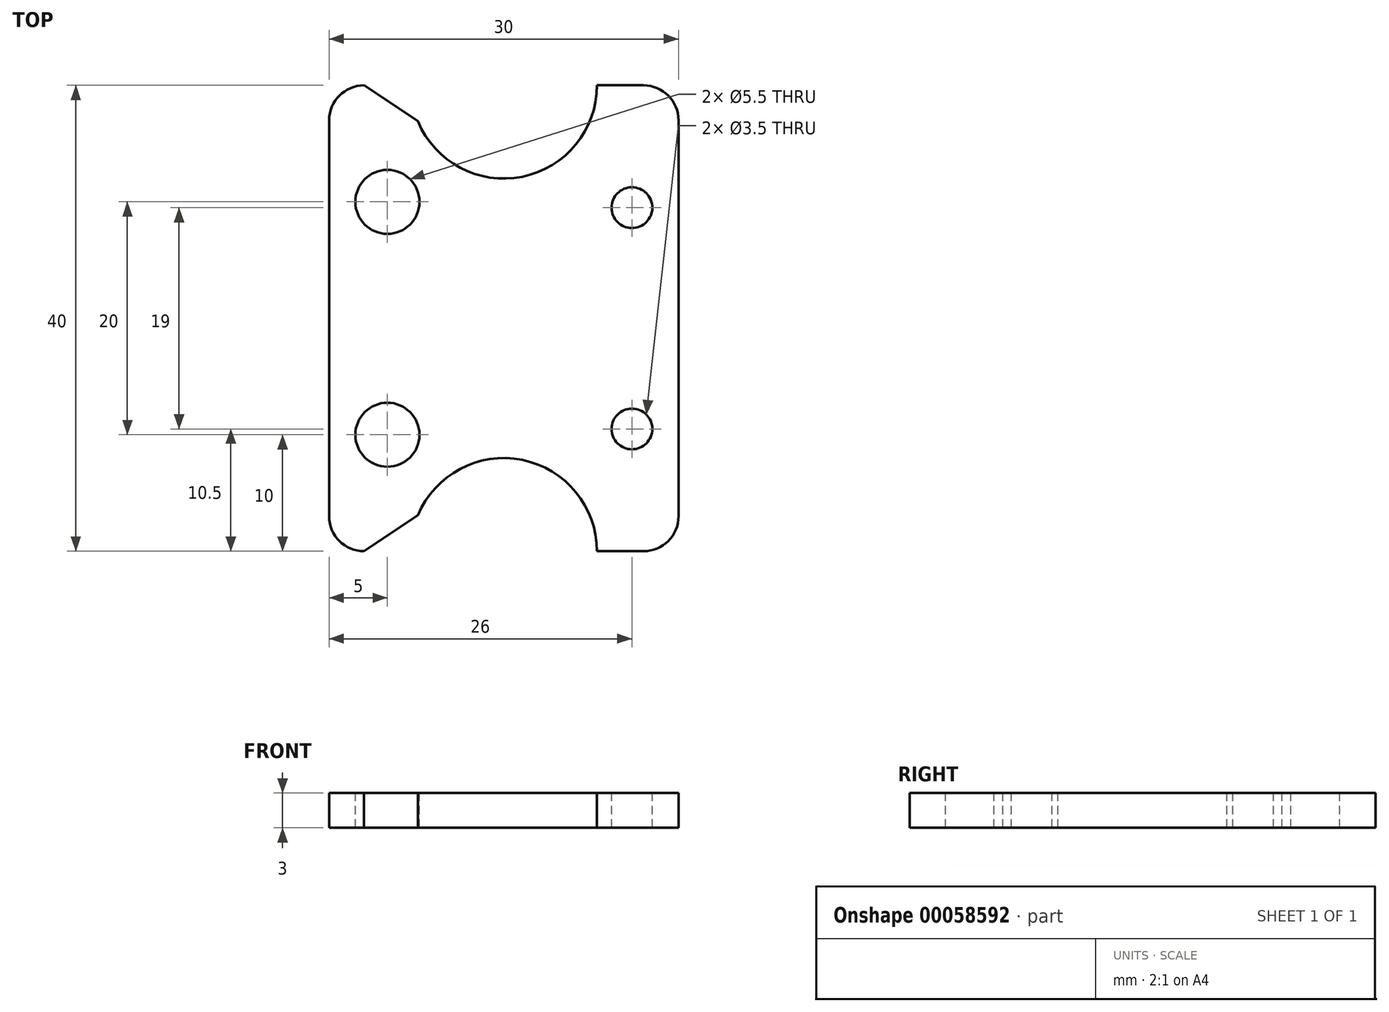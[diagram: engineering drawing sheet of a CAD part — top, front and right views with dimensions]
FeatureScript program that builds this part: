
annotation { "Feature Type Name" : "Feature", "Feature Type Description" : "" }
export const myFeature = defineFeature(function(context is Context, id is Id, definition is map)
    precondition{}
    {
        {
            var Q0;
            Q0=qCreatedBy(makeId("Top.planeOp"),FACE);
            var sketch = newSketch(context, id + "F5", { "sketchPlane" : qUnion([Q0])});
            skLineSegment(sketch, "E0.rect.bottom", {"start": v(15, -20) * mm, "end": v(-15, -20) * mm});
            skLineSegment(sketch, "E0.rect.top", {"start": v(15, 20) * mm, "end": v(-15, 20) * mm});
            skLineSegment(sketch, "E0.rect.left", {"start": v(15, -20) * mm, "end": v(15, 20) * mm});
            skLineSegment(sketch, "E0.rect.right", {"start": v(-15, -20) * mm, "end": v(-15, 20) * mm});
            skPoint(sketch, "E0.rect.middle", {"position": v(0, 0) * mm});
            skSolve(sketch);
        }
        {
            var Q0;
            Q0=makeQuery(id+"F5.imprint","IMPRINT",FACE,{"disambiguationData":[TD([[makeQuery(id+"F5.imprint","IMPRINT",EDGE,{"derivedFrom":sQuery(id+"F5.wireOp",EDGE,"E0.rect.bottom")}),-1.0]])]});
            extrude(context, id + "F6", {"entities" : qUnion([Q0]), "depth" : 3 * mm});
        }
        {
            var Q0;
            Q0=makeQuery(id+"F6.opExtrude","CAP_FACE",FACE,{"disambiguationData":[OSD([sQuery(id+"F5.wireOp",EDGE,"E0.rect.bottom"),sQuery(id+"F5.wireOp",EDGE,"E0.rect.top"),sQuery(id+"F5.wireOp",EDGE,"E0.rect.left"),sQuery(id+"F5.wireOp",EDGE,"E0.rect.right")])],"isStart":false});
            var sketch = newSketch(context, id + "F7", { "sketchPlane" : qUnion([Q0])});
            skPoint(sketch, "E1", {"position": v(-10, 10) * mm});
            skPoint(sketch, "E2", {"position": v(-10, -10) * mm});
            skPoint(sketch, "E3", {"position": v(11, 9.5) * mm});
            skPoint(sketch, "E4", {"position": v(11, -9.5) * mm});
            skSolve(sketch);
        }
        {
            var Q0;
            Q0=sQuery(id+"F7.wireOp",VERTEX,"E1");
            var Q1;
            Q1=sQuery(id+"F7.wireOp",VERTEX,"E2");
            var Q2;
            Q2=makeQuery(id+"F6.opExtrude","SWEPT_BODY",BODY,{"disambiguationData":[OSD([sQuery(id+"F5.wireOp",EDGE,"E0.rect.bottom"),sQuery(id+"F5.wireOp",EDGE,"E0.rect.top"),sQuery(id+"F5.wireOp",EDGE,"E0.rect.left"),sQuery(id+"F5.wireOp",EDGE,"E0.rect.right")])]});
            hole(context, id + "F8", {"style" : HoleStyle.SIMPLE, "holeDiameter" : 5.5 * mm, "endStyle" : HoleEndStyle.THROUGH, "locations" : qUnion([Q0, Q1]), "scope" : qUnion([Q2])});
        }
        {
            var Q0;
            Q0=sQuery(id+"F7.wireOp",VERTEX,"E3");
            var Q1;
            Q1=sQuery(id+"F7.wireOp",VERTEX,"E4");
            var Q2;
            Q2=makeQuery(id+"F6.opExtrude","SWEPT_BODY",BODY,{"disambiguationData":[OSD([sQuery(id+"F5.wireOp",EDGE,"E0.rect.bottom"),sQuery(id+"F5.wireOp",EDGE,"E0.rect.top"),sQuery(id+"F5.wireOp",EDGE,"E0.rect.left"),sQuery(id+"F5.wireOp",EDGE,"E0.rect.right")])]});
            hole(context, id + "F9", {"style" : HoleStyle.SIMPLE, "holeDiameter" : 3.5 * mm, "endStyle" : HoleEndStyle.THROUGH, "locations" : qUnion([Q0, Q1]), "scope" : qUnion([Q2])});
        }
        {
            var Q0;
            Q0=makeQuery(id+"F7.imprint","IMPRINT",FACE,{"disambiguationData":[TD([[makeQuery(id+"F7.imprint","IMPRINT",EDGE,{"derivedFrom":makeQuery(id+"F6.opExtrude","CAP_EDGE",EDGE,{"disambiguationData":[OSD([sQuery(id+"F5.wireOp",EDGE,"E0.rect.bottom")])],"isStart":false})}),-1.0]])]});
            var sketch = newSketch(context, id + "F0", { "sketchPlane" : qUnion([Q0])});
            skCircle(sketch, "E5", {"center": v(0, -20) * mm, "radius": 8 * mm});
            skCircle(sketch, "E6", {"center": v(0, 20) * mm, "radius": 8 * mm});
            skSolve(sketch);
        }
        {
            var Q0;
            {var subQ0=sQuery(id+"F0.wireOp",EDGE,"E5");var subQ1=makeQuery(id+"F7.imprint","IMPRINT",EDGE,{"derivedFrom":makeQuery(id+"F6.opExtrude","CAP_EDGE",EDGE,{"disambiguationData":[OSD([sQuery(id+"F5.wireOp",EDGE,"E0.rect.bottom")])],"isStart":false})});var subQ2=makeQuery(id+"F0.imprint","INTERSECT",VERTEX,{"disambiguationData":[OD(0.0)],"derivedFrom":[subQ1,subQ0]});Q0=makeQuery(id+"F0.imprint","IMPRINT",FACE,{"disambiguationData":[TD([[makeQuery(id+"F0.imprint","IMPRINT",EDGE,{"disambiguationData":[TD([[subQ2,-1.0]])],"derivedFrom":subQ0}),1.0]])]});}
            var Q1;
            {var subQ0=sQuery(id+"F0.wireOp",EDGE,"E6");var subQ1=makeQuery(id+"F7.imprint","IMPRINT",EDGE,{"derivedFrom":makeQuery(id+"F6.opExtrude","CAP_EDGE",EDGE,{"disambiguationData":[OSD([sQuery(id+"F5.wireOp",EDGE,"E0.rect.top")])],"isStart":false})});var subQ2=makeQuery(id+"F0.imprint","INTERSECT",VERTEX,{"disambiguationData":[OD(0.0)],"derivedFrom":[subQ1,subQ0]});Q1=makeQuery(id+"F0.imprint","IMPRINT",FACE,{"disambiguationData":[TD([[makeQuery(id+"F0.imprint","IMPRINT",EDGE,{"disambiguationData":[TD([[subQ2,1.0]])],"derivedFrom":subQ0}),1.0]])]});}
            extrude(context, id + "F1", {"entities" : qUnion([Q0, Q1]), "operationType" : NewBodyOperationType.REMOVE, "oppositeDirection" : true, "depth" : 25 * mm});
        }
        {
            var Q0;
            Q0=makeQuery(id+"F6.opExtrude","SWEPT_EDGE",EDGE,{"disambiguationData":[OSD([sQuery(id+"F5.wireOp",EDGE,"E0.rect.bottom"),sQuery(id+"F5.wireOp",EDGE,"E0.rect.left")])]});
            var Q1;
            Q1=makeQuery(id+"F6.opExtrude","SWEPT_EDGE",EDGE,{"disambiguationData":[OSD([sQuery(id+"F5.wireOp",EDGE,"E0.rect.bottom"),sQuery(id+"F5.wireOp",EDGE,"E0.rect.right")])]});
            var Q2;
            Q2=makeQuery(id+"F6.opExtrude","SWEPT_EDGE",EDGE,{"disambiguationData":[OSD([sQuery(id+"F5.wireOp",EDGE,"E0.rect.top"),sQuery(id+"F5.wireOp",EDGE,"E0.rect.left")])]});
            var Q3;
            Q3=makeQuery(id+"F6.opExtrude","SWEPT_EDGE",EDGE,{"disambiguationData":[OSD([sQuery(id+"F5.wireOp",EDGE,"E0.rect.top"),sQuery(id+"F5.wireOp",EDGE,"E0.rect.right")])]});
            fillet(context, id + "F2", {"entities" : qUnion([Q0, Q1, Q2, Q3]), "radius" : 3 * mm, "tangentPropagation" : true, "allowEdgeOverflow" : false});
        }
        {
            var Q0;
            {var subQ0=sQuery(id+"F0.wireOp",EDGE,"E6");var subQ1=sQuery(id+"F5.wireOp",EDGE,"E0.rect.top");Q0=makeQuery(id+"F1.boolean.opBoolean","COPY",EDGE,{"derivedFrom":makeQuery(id+"F1.opExtrude","SWEPT_EDGE",EDGE,{"disambiguationData":[OSD([subQ1,subQ0]),TDD([makeQuery(id+"F0.imprint","INTERSECT",VERTEX,{"disambiguationData":[OD(1.0)],"derivedFrom":[makeQuery(id+"F7.imprint","IMPRINT",EDGE,{"derivedFrom":makeQuery(id+"F6.opExtrude","CAP_EDGE",EDGE,{"disambiguationData":[OSD([subQ1])],"isStart":false})}),subQ0]})])]})});}
            var Q1;
            {var subQ0=sQuery(id+"F0.wireOp",EDGE,"E6");var subQ1=sQuery(id+"F5.wireOp",EDGE,"E0.rect.top");Q1=makeQuery(id+"F1.boolean.opBoolean","COPY",EDGE,{"derivedFrom":makeQuery(id+"F1.opExtrude","SWEPT_EDGE",EDGE,{"disambiguationData":[OSD([subQ1,subQ0]),TDD([makeQuery(id+"F0.imprint","INTERSECT",VERTEX,{"disambiguationData":[OD(0.0)],"derivedFrom":[makeQuery(id+"F7.imprint","IMPRINT",EDGE,{"derivedFrom":makeQuery(id+"F6.opExtrude","CAP_EDGE",EDGE,{"disambiguationData":[OSD([subQ1])],"isStart":false})}),subQ0]})])]})});}
            chamfer(context, id + "F3", {"entities" : qUnion([Q0, Q1]), "width" : 5 * mm, "tangentPropagation" : true});
        }
        {
            var Q0;
            {var subQ0=sQuery(id+"F0.wireOp",EDGE,"E5");var subQ1=sQuery(id+"F5.wireOp",EDGE,"E0.rect.bottom");Q0=makeQuery(id+"F1.boolean.opBoolean","COPY",EDGE,{"derivedFrom":makeQuery(id+"F1.opExtrude","SWEPT_EDGE",EDGE,{"disambiguationData":[OSD([subQ1,subQ0]),TDD([makeQuery(id+"F0.imprint","INTERSECT",VERTEX,{"disambiguationData":[OD(0.0)],"derivedFrom":[makeQuery(id+"F7.imprint","IMPRINT",EDGE,{"derivedFrom":makeQuery(id+"F6.opExtrude","CAP_EDGE",EDGE,{"disambiguationData":[OSD([subQ1])],"isStart":false})}),subQ0]})])]})});}
            var Q1;
            {var subQ0=sQuery(id+"F0.wireOp",EDGE,"E5");var subQ1=sQuery(id+"F5.wireOp",EDGE,"E0.rect.bottom");Q1=makeQuery(id+"F1.boolean.opBoolean","COPY",EDGE,{"derivedFrom":makeQuery(id+"F1.opExtrude","SWEPT_EDGE",EDGE,{"disambiguationData":[OSD([subQ1,subQ0]),TDD([makeQuery(id+"F0.imprint","INTERSECT",VERTEX,{"disambiguationData":[OD(1.0)],"derivedFrom":[makeQuery(id+"F7.imprint","IMPRINT",EDGE,{"derivedFrom":makeQuery(id+"F6.opExtrude","CAP_EDGE",EDGE,{"disambiguationData":[OSD([subQ1])],"isStart":false})}),subQ0]})])]})});}
            chamfer(context, id + "F4", {"entities" : qUnion([Q0, Q1]), "width" : 5 * mm, "tangentPropagation" : true});
        }
    });
